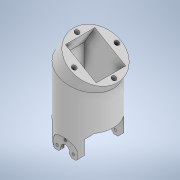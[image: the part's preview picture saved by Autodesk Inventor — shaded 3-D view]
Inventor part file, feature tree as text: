
AUTODESK INVENTOR PART (.ipt)
format: ipt  version: 2022 (Build 260153000, 153)  size: 277,504 bytes
history: native  units: mm
features: extrude x7, sketch x4, sweep x1, plane x1, mirror x1, chamfer x1, projected_geometry x1
ambient origin geometry x8: Origin, YZ Plane, XZ Plane, XY Plane, X Axis, Y Axis, Z Axis, Center Point
bodies: Body1 (feature_tree)
feature tree (16):
  sweep  "Sweep1"
  extrude  "Extrusion2"  Depth=15.0mm
  extrude  "Extrusion3"  Depth=20.5mm
  extrude  "Extrusion4"  TaperAngle=0.0deg  [1 undecoded]
  extrude  "Extrusion6"  Depth=35.0mm TaperAngle=0.0deg
  plane  "Work Plane1"
  extrude  "Extrusion7"  Depth=35.0mm TaperAngle=0.0deg
  mirror  "Mirror1"
  extrude  "Extrusion8"  Depth=38.4mm TaperAngle=0.0deg
  chamfer  "Chamfer4"  Distance=8.5mm
  extrude  "Extrusion12"  Depth=35.0mm TaperAngle=0.0deg
  sketch  "Sketch2"  dims[d0=50.0mm d3=150.0deg]
  sketch  "Sketch7"  dims[d4=40.0mm d5=15.0mm]
  sketch  "Sketch8"  dims[d6=0.0mm d7=0.0mm d8=20.5mm]
  projected_geometry  "Projected Loop1"
  sketch  "Sketch14"  dims[d9=20.0mm d10=0.0mm d11=50.0mm d12=0.0mm d14=50.0mm d15=0.0mm d18=38.4mm d19=0.0mm d26=8.5mm d32=50.0mm d33=0.0mm d34=25.0mm d35=25.0mm d36=2.8mm d37=0.0mm d41=2.5mm d49=21.0mm d50=4.4mm d51=40.0mm d53=360.0deg d55=7.0mm d56=0.0mm d57=0.0mm d58=40.0mm d60=360.0deg d62=35.0mm d63=17.5mm d64=29.0mm d65=14.5mm d87=4.7mm d88=2.0mm d89=45.0deg d94=40.0mm d95=15.0deg d96=60.0deg d98=5.0mm d112=50.0mm d113=80.0mm d114=2.0mm d115=135.0deg d116=135.0deg d117=50.0mm d118=0.0mm d119=135.0deg d120=135.0deg]
note: 1 required parameter value undecoded (feature->parameter linkage not recoverable at this tier; creation-order binding heuristic only, values carry confidence <= 0.55)
